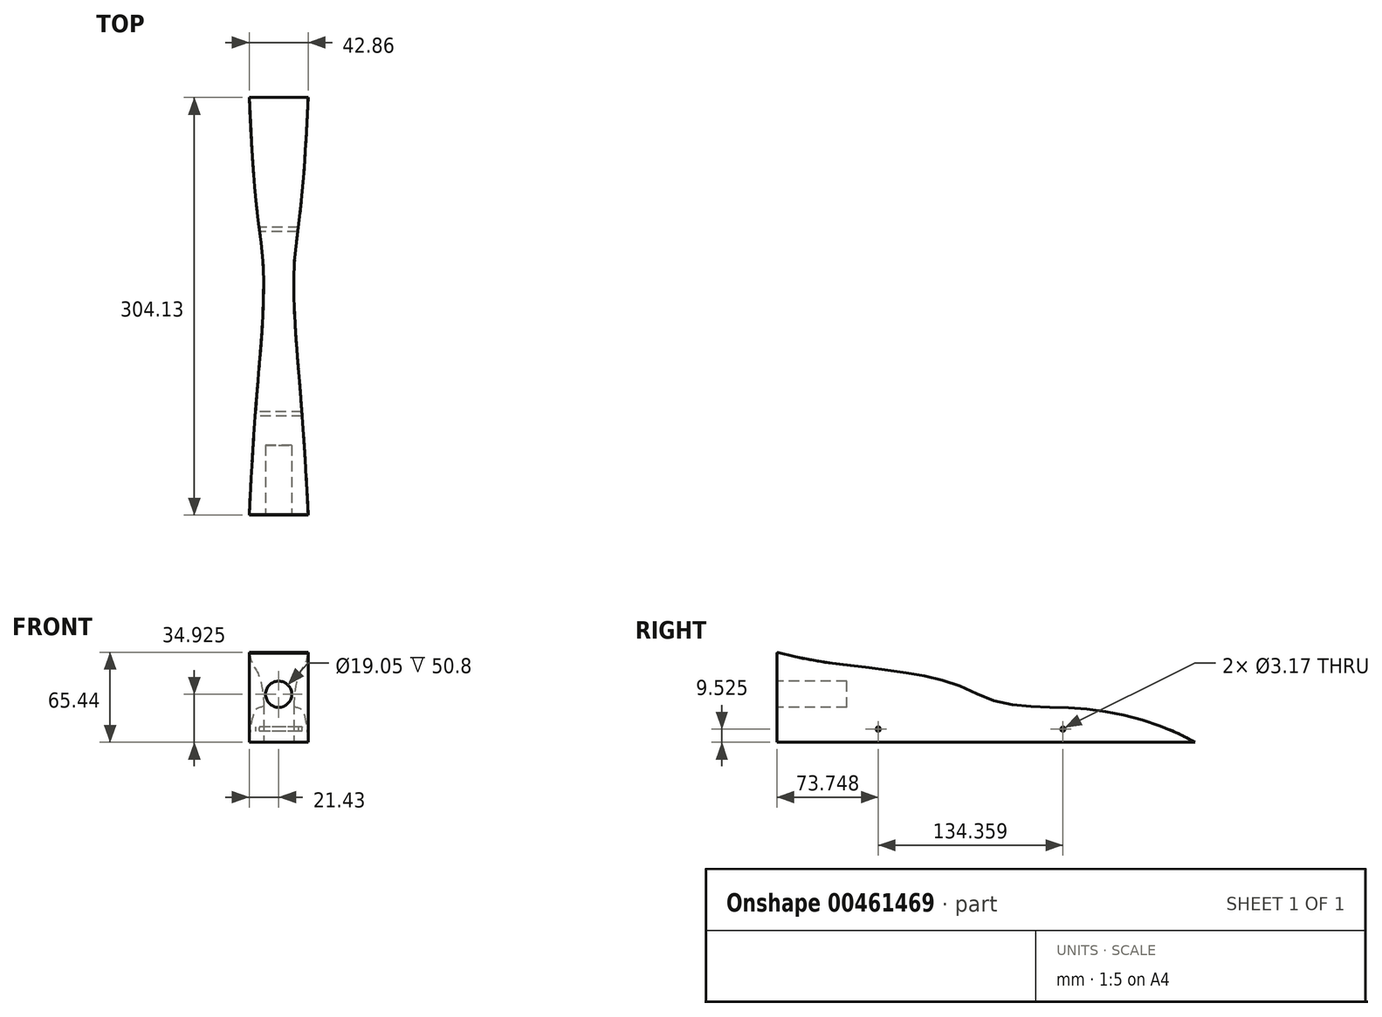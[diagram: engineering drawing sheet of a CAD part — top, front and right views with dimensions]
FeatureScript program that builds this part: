
annotation { "Feature Type Name" : "Feature", "Feature Type Description" : "" }
export const myFeature = defineFeature(function(context is Context, id is Id, definition is map)
    precondition{}
    {
        {
            var Q0;
            Q0=qCreatedBy(makeId("Right.planeOp"),FACE);
            var sketch = newSketch(context, id + "F0", { "sketchPlane" : qUnion([Q0])});
            skLineSegment(sketch, "E0", {"start": v(-152.4, 0) * mm, "end": v(152.4, 0) * mm});
            skLineSegment(sketch, "E1", {"start": v(-152.4, 0) * mm, "end": v(-152.4, 69.85) * mm});
            skLineSegment(sketch, "E2", {"start": v(152.4, 0) * mm, "end": v(152.4, 19.05) * mm});
            skLineSegment(sketch, "E3", {"start": v(152.4, 19.05) * mm, "end": v(-152.4, 69.85) * mm});
            skPoint(sketch, "E4.endSnap0", {"position": v(-152.4, 34.93) * mm});
            skLineSegment(sketch, "E5.0", {"start": v(-95.25, 50.8) * mm, "end": v(-152.4, 50.8) * mm, "construction": true});
            skLineSegment(sketch, "E5.1", {"start": v(-95.25, 50.8) * mm, "end": v(-95.25, 19.05) * mm, "construction": true});
            skLineSegment(sketch, "E5.2", {"start": v(-95.25, 19.05) * mm, "end": v(-152.4, 19.05) * mm, "construction": true});
            skSolve(sketch);
        }
        {
            var Q0;
            Q0=makeQuery(id+"F0.imprint","IMPRINT",FACE,{"disambiguationData":[TD([[makeQuery(id+"F0.imprint","IMPRINT",EDGE,{"derivedFrom":sQuery(id+"F0.wireOp",EDGE,"E0")}),1.0]])]});
            extrude(context, id + "F1", {"entities" : qUnion([Q0]), "depth" : 42.86 * mm, "symmetric" : true});
        }
        {
            var Q0;
            Q0=makeQuery(id+"F1.opExtrude","SWEPT_FACE",FACE,{"disambiguationData":[OSD([sQuery(id+"F0.wireOp",EDGE,"E1")])]});
            var sketch = newSketch(context, id + "F2", { "sketchPlane" : qUnion([Q0])});
            skLineSegment(sketch, "E6", {"start": v(21.43, 34.93) * mm, "end": v(0, 34.93) * mm, "construction": true});
            skCircle(sketch, "E7", {"center": v(0, 34.93) * mm, "radius": 9.53 * mm});
            skSolve(sketch);
        }
        {
            var Q0;
            Q0=makeQuery(id+"F2.imprint","IMPRINT",FACE,{"disambiguationData":[TD([[makeQuery(id+"F2.imprint","IMPRINT",EDGE,{"derivedFrom":sQuery(id+"F2.wireOp",EDGE,"E7")}),1.0]])]});
            var Q1;
            Q1=sQuery(id+"F2.wireOp",EDGE,"E7");
            extrude(context, id + "F3", {"entities" : qUnion([Q0]), "operationType" : NewBodyOperationType.REMOVE, "surfaceEntities" : qUnion([Q1]), "oppositeDirection" : true, "depth" : 50.8 * mm});
        }
        {
            var Q0;
            Q0=makeQuery(id+"F1.opExtrude","CAP_FACE",FACE,{"disambiguationData":[OSD([sQuery(id+"F0.wireOp",EDGE,"E0"),sQuery(id+"F0.wireOp",EDGE,"E1"),sQuery(id+"F0.wireOp",EDGE,"E2"),sQuery(id+"F0.wireOp",EDGE,"E3")])],"isStart":false});
            var sketch = newSketch(context, id + "F4", { "sketchPlane" : qUnion([Q0])});
            skLineSegment(sketch, "E8", {"start": v(-152.4, 34.93) * mm, "end": v(-152.4, 44.45) * mm, "construction": true});
            skLineSegment(sketch, "E9.0", {"start": v(-95.25, 19.05) * mm, "end": v(-152.4, 19.05) * mm, "construction": true});
            skLineSegment(sketch, "E9.1", {"start": v(-95.25, 50.8) * mm, "end": v(-95.25, 19.05) * mm, "construction": true});
            skLineSegment(sketch, "E9.2", {"start": v(-152.4, 50.8) * mm, "end": v(-95.25, 50.8) * mm, "construction": true});
            skLineSegment(sketch, "E10", {"start": v(57.15, 0) * mm, "end": v(57.15, 34.93) * mm, "construction": true});
            skLineSegment(sketch, "E11", {"start": v(-152.4, 44.45) * mm, "end": v(-101.6, 44.45) * mm, "construction": true});
            skLineSegment(sketch, "E12", {"start": v(-101.6, 44.45) * mm, "end": v(-101.6, 25.4) * mm, "construction": true});
            skLineSegment(sketch, "E13", {"start": v(-101.6, 25.4) * mm, "end": v(-152.4, 25.4) * mm, "construction": true});
            skCircle(sketch, "E14", {"center": v(57.15, 9.53) * mm, "radius": 1.59 * mm});
            skCircle(sketch, "E15", {"center": v(-78.65, 9.53) * mm, "radius": 1.59 * mm});
            skSolve(sketch);
        }
        {
            var Q0;
            Q0=makeQuery(id+"F1.opExtrude","SWEPT_FACE",FACE,{"disambiguationData":[OSD([sQuery(id+"F0.wireOp",EDGE,"E0")])]});
            var sketch = newSketch(context, id + "F5", { "sketchPlane" : qUnion([Q0])});
            skLineSegment(sketch, "E16", {"start": v(0, 152.4) * mm, "end": v(0, -152.4) * mm, "construction": true});
            skLineSegment(sketch, "E17", {"start": v(21.43, -57.22) * mm, "end": v(-21.43, -57.22) * mm, "construction": true});
            skLineSegment(sketch, "E18", {"start": v(15.88, 152.4) * mm, "end": v(15.88, 95.25) * mm, "construction": true});
            skLineSegment(sketch, "E19", {"start": v(15.88, 95.25) * mm, "end": v(-15.87, 95.25) * mm, "construction": true});
            skLineSegment(sketch, "E20", {"start": v(-15.87, 95.25) * mm, "end": v(-15.87, 152.4) * mm, "construction": true});
            skLineSegment(sketch, "E21", {"start": v(0, 152.4) * mm, "end": v(-9.53, 152.4) * mm, "construction": true});
            skLineSegment(sketch, "E22", {"start": v(-9.53, 152.4) * mm, "end": v(-9.53, 101.6) * mm, "construction": true});
            skLineSegment(sketch, "E23", {"start": v(-9.52, 101.6) * mm, "end": v(9.53, 101.6) * mm, "construction": true});
            skLineSegment(sketch, "E24", {"start": v(9.53, 101.6) * mm, "end": v(9.53, 152.4) * mm, "construction": true});
            skPoint(sketch, "E25.4.internal.orphan", {"position": v(15.88, 19.52) * mm});
            skPoint(sketch, "E25.6.internal.orphan", {"position": v(15.88, -14.84) * mm});
            skPoint(sketch, "E25.8.internal.orphan", {"position": v(15.88, -89.13) * mm});
            skFitSpline(sketch, "E26", {"points": [v(21.43, 152.4) * mm, v(15.88, 64.65) * mm, v(10.95, -20.93) * mm, v(15.88, -70.48) * mm, v(21.43, -152.4) * mm], "startDerivative": vector(-14.73, -318.48) * mm, "endDerivative": vector(14.06, -341.02) * mm});
            skFitSpline(sketch, "E27.MirrorCS", {"points": [v(-21.43, 152.4) * mm, v(-15.88, 64.65) * mm, v(-10.95, -20.93) * mm, v(-15.88, -70.48) * mm, v(-21.43, -152.4) * mm], "startDerivative": vector(14.73, -318.48) * mm, "endDerivative": vector(-14.06, -341.02) * mm});
            skSolve(sketch);
        }
        {
            var Q0;
            Q0=qCreatedBy(makeId("Right.planeOp"),FACE);
            var sketch = newSketch(context, id + "F6", { "sketchPlane" : qUnion([Q0])});
            skFitSpline(sketch, "E28", {"points": [v(151.73, 0) * mm, v(77.27, 23.67) * mm, v(10.16, 28.8) * mm, v(-28.02, 44.06) * mm, v(-121.18, 58.87) * mm, v(-152.02, 65.44) * mm], "startDerivative": vector(-289.49, 166.75) * mm, "endDerivative": vector(-162.63, 36.14) * mm});
            skLineSegment(sketch, "E29", {"start": v(-152.02, 65.44) * mm, "end": v(-173.6, 22.93) * mm});
            skLineSegment(sketch, "E30", {"start": v(-173.6, 22.93) * mm, "end": v(-173.6, -33.52) * mm});
            skLineSegment(sketch, "E31", {"start": v(-173.6, -33.52) * mm, "end": v(174.22, -16.3) * mm});
            skLineSegment(sketch, "E32", {"start": v(174.22, -16.3) * mm, "end": v(151.73, 0) * mm});
            skCircle(sketch, "E33", {"center": v(55.7, 9.53) * mm, "radius": 1.59 * mm});
            skPoint(sketch, "E34.0", {"position": v(-78.65, 9.53) * mm});
            skCircle(sketch, "E35.0", {"center": v(-78.65, 9.53) * mm, "radius": 1.59 * mm});
            skSolve(sketch);
        }
        {
            var Q0;
            Q0 = qSketchRegion(id + "F6", true);
            extrude(context, id + "F7", {"entities" : qUnion([Q0]), "operationType" : NewBodyOperationType.INTERSECT, "endBound" : BoundingType.THROUGH_ALL, "depth" : 25.4 * mm, "hasSecondDirection" : true, "secondDirectionBound" : BoundingType.THROUGH_ALL, "secondDirectionOppositeDirection" : true, "secondDirectionDepth" : 25.4 * mm});
        }
        {
            var Q0;
            Q0=makeQuery(id+"F5.imprint","IMPRINT",FACE,{"disambiguationData":[TD([[makeQuery(id+"F5.imprint","IMPRINT",EDGE,{"derivedFrom":sQuery(id+"F5.wireOp",EDGE,"E27.MirrorCS")}),-1.0]])]});
            var Q1;
            Q1=makeQuery(id+"F5.imprint","IMPRINT",FACE,{"disambiguationData":[TD([[makeQuery(id+"F5.imprint","IMPRINT",EDGE,{"derivedFrom":sQuery(id+"F5.wireOp",EDGE,"E26")}),1.0]])]});
            extrude(context, id + "F8", {"entities" : qUnion([Q0, Q1]), "operationType" : NewBodyOperationType.REMOVE, "endBound" : BoundingType.THROUGH_ALL, "oppositeDirection" : true, "depth" : 25.4 * mm});
        }
    });
